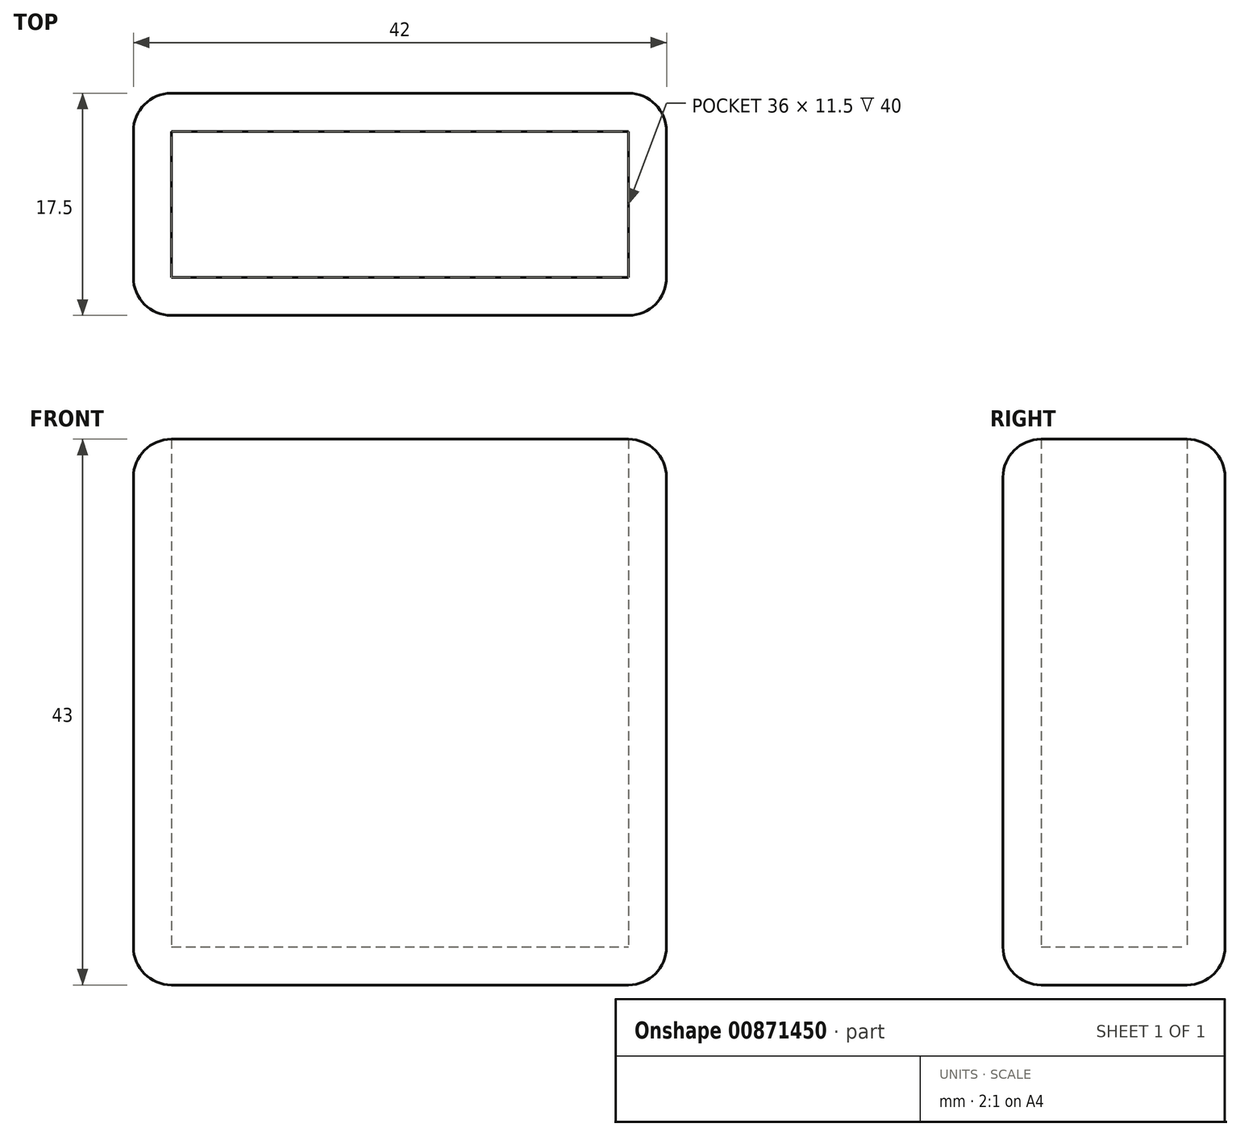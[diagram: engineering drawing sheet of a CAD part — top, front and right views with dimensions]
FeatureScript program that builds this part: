
annotation { "Feature Type Name" : "Feature", "Feature Type Description" : "" }
export const myFeature = defineFeature(function(context is Context, id is Id, definition is map)
    precondition{}
    {
        {
            var Q0;
            Q0=qCreatedBy(makeId("Top.planeOp"),FACE);
            var sketch = newSketch(context, id + "F0", { "sketchPlane" : qUnion([Q0])});
            skLineSegment(sketch, "E0.bottom", {"start": v(-5.86, -8.87) * mm, "end": v(30.14, -8.87) * mm});
            skLineSegment(sketch, "E0.top", {"start": v(-5.86, 2.63) * mm, "end": v(30.14, 2.63) * mm});
            skLineSegment(sketch, "E0.left", {"start": v(-5.86, -8.87) * mm, "end": v(-5.86, 2.63) * mm});
            skLineSegment(sketch, "E0.right", {"start": v(30.14, -8.87) * mm, "end": v(30.14, 2.63) * mm});
            skLineSegment(sketch, "E1.bottom", {"start": v(-8.86, -11.87) * mm, "end": v(33.14, -11.87) * mm});
            skLineSegment(sketch, "E1.top", {"start": v(-8.86, 5.63) * mm, "end": v(33.14, 5.63) * mm});
            skLineSegment(sketch, "E1.left", {"start": v(-8.86, -11.87) * mm, "end": v(-8.86, 5.63) * mm});
            skLineSegment(sketch, "E1.right", {"start": v(33.14, -11.87) * mm, "end": v(33.14, 5.63) * mm});
            skSolve(sketch);
        }
        {
            var Q0;
            Q0=makeQuery(id+"F0.imprint","IMPRINT",FACE,{"disambiguationData":[TD([[makeQuery(id+"F0.imprint","IMPRINT",EDGE,{"derivedFrom":sQuery(id+"F0.wireOp",EDGE,"E0.bottom")}),-1.0]])]});
            extrude(context, id + "F1", {"entities" : qUnion([Q0]), "depth" : 40 * mm, "offsetDistance" : 25 * mm});
        }
        {
            var Q0;
            Q0=makeQuery(id+"F0.imprint","IMPRINT",FACE,{"disambiguationData":[TD([[makeQuery(id+"F0.imprint","IMPRINT",EDGE,{"derivedFrom":sQuery(id+"F0.wireOp",EDGE,"E0.bottom")}),-1.0]])]});
            var Q1;
            Q1=makeQuery(id+"F0.imprint","IMPRINT",FACE,{"disambiguationData":[TD([[makeQuery(id+"F0.imprint","IMPRINT",EDGE,{"derivedFrom":sQuery(id+"F0.wireOp",EDGE,"E0.bottom")}),1.0]])]});
            extrude(context, id + "F2", {"entities" : qUnion([Q0, Q1]), "operationType" : NewBodyOperationType.ADD, "oppositeDirection" : true, "depth" : 3 * mm, "offsetDistance" : 25 * mm});
        }
        {
            var Q0;
            {var subQ0=sQuery(id+"F0.wireOp",EDGE,"E1.right");var subQ1=sQuery(id+"F0.wireOp",EDGE,"E1.bottom");Q0=makeQuery(id+"F2.boolean.opBoolean","MERGE",EDGE,{"derivedFrom":[makeQuery(id+"F1.opExtrude","SWEPT_EDGE",EDGE,{"disambiguationData":[OSD([subQ1,subQ0])]}),makeQuery(id+"F2.opExtrude","SWEPT_EDGE",EDGE,{"disambiguationData":[OSD([subQ1,subQ0])]})]});}
            var Q1;
            Q1=makeQuery(id+"F2.opExtrude","CAP_EDGE",EDGE,{"disambiguationData":[OSD([sQuery(id+"F0.wireOp",EDGE,"E1.bottom")])],"isStart":false});
            var Q2;
            Q2=makeQuery(id+"F2.opExtrude","CAP_EDGE",EDGE,{"disambiguationData":[OSD([sQuery(id+"F0.wireOp",EDGE,"E1.right")])],"isStart":false});
            var Q3;
            {var subQ0=sQuery(id+"F0.wireOp",EDGE,"E1.right");var subQ1=sQuery(id+"F0.wireOp",EDGE,"E1.top");Q3=makeQuery(id+"F2.boolean.opBoolean","MERGE",EDGE,{"derivedFrom":[makeQuery(id+"F1.opExtrude","SWEPT_EDGE",EDGE,{"disambiguationData":[OSD([subQ1,subQ0])]}),makeQuery(id+"F2.opExtrude","SWEPT_EDGE",EDGE,{"disambiguationData":[OSD([subQ1,subQ0])]})]});}
            var Q4;
            Q4=makeQuery(id+"F2.opExtrude","CAP_EDGE",EDGE,{"disambiguationData":[OSD([sQuery(id+"F0.wireOp",EDGE,"E1.top")])],"isStart":false});
            var Q5;
            {var subQ0=sQuery(id+"F0.wireOp",EDGE,"E1.left");var subQ1=sQuery(id+"F0.wireOp",EDGE,"E1.top");Q5=makeQuery(id+"F2.boolean.opBoolean","MERGE",EDGE,{"derivedFrom":[makeQuery(id+"F1.opExtrude","SWEPT_EDGE",EDGE,{"disambiguationData":[OSD([subQ1,subQ0])]}),makeQuery(id+"F2.opExtrude","SWEPT_EDGE",EDGE,{"disambiguationData":[OSD([subQ1,subQ0])]})]});}
            var Q6;
            Q6=makeQuery(id+"F2.opExtrude","CAP_EDGE",EDGE,{"disambiguationData":[OSD([sQuery(id+"F0.wireOp",EDGE,"E1.left")])],"isStart":false});
            var Q7;
            {var subQ0=sQuery(id+"F0.wireOp",EDGE,"E1.left");var subQ1=sQuery(id+"F0.wireOp",EDGE,"E1.bottom");Q7=makeQuery(id+"F2.boolean.opBoolean","MERGE",EDGE,{"derivedFrom":[makeQuery(id+"F1.opExtrude","SWEPT_EDGE",EDGE,{"disambiguationData":[OSD([subQ1,subQ0])]}),makeQuery(id+"F2.opExtrude","SWEPT_EDGE",EDGE,{"disambiguationData":[OSD([subQ1,subQ0])]})]});}
            fillet(context, id + "F3", {"entities" : qUnion([Q0, Q1, Q2, Q3, Q4, Q5, Q6, Q7]), "radius" : 3 * mm, "tangentPropagation" : true, "allowEdgeOverflow" : false});
        }
        {
            var Q0;
            Q0=makeQuery(id+"F1.opExtrude","CAP_EDGE",EDGE,{"disambiguationData":[OSD([sQuery(id+"F0.wireOp",EDGE,"E1.top")])],"isStart":false});
            var Q1;
            Q1=makeQuery(id+"F1.opExtrude","CAP_EDGE",EDGE,{"disambiguationData":[OSD([sQuery(id+"F0.wireOp",EDGE,"E1.left")])],"isStart":false});
            var Q2;
            Q2=makeQuery(id+"F1.opExtrude","CAP_EDGE",EDGE,{"disambiguationData":[OSD([sQuery(id+"F0.wireOp",EDGE,"E1.bottom")])],"isStart":false});
            var Q3;
            Q3=makeQuery(id+"F1.opExtrude","CAP_EDGE",EDGE,{"disambiguationData":[OSD([sQuery(id+"F0.wireOp",EDGE,"E1.right")])],"isStart":false});
            fillet(context, id + "F4", {"entities" : qUnion([Q0, Q1, Q2, Q3]), "radius" : 3 * mm, "tangentPropagation" : true, "allowEdgeOverflow" : false});
        }
    });
